# Revit family: Electronics_Desono_Biamp_Full-Range-Surface-Mount-Loudspeaker_KUBO3_KUBO3T
name_source: partatom
category: Communication Devices
units: mm (PartAtom-declared; Revit-internal decimal feet)

## family parameters
Cut with Voids When Loaded = No
Host = Face
Maintain Annotation Orientation = No
OmniClass Number = 23.85.10.11.14.14.14
Part Type = Normal
Room Calculation Point = No
Round Connector Dimension = Use Diameter
Shared = No

## types (4) — shared parameters
Default Elevation = 4' - 0"
Depth = 0' - 4 1/2"
Environmental = IP40 per IEC 60529
Height = 0' - 5"
Input Connection = (2x) 2-way Euroblock connectors for daisy-chaining;connectors accept up to 12 AWG (2.5 mm²)conductors
Manufacturer = Biamp
Mounting Provisions = U-bracket
Nominal Beamwidth  (H x V) = 100° x 100°
Operating Environment = Indoor
Operating Mode = Passive
Operating Range (-10dB) = 115 Hz to 20 kHz
Product Documentation Link = https://downloads.biamp.com
Product Page URL = https://www.biamp.com
Product data url = https://www.bimobject.com
Protection = 3-step self-resetting protection
Transducers = 1 x 3 (76 mm) polypropylene cone
URL = https://www.biamp.com
Width = 0' - 5"

## per-type parameters (varying)
| type | Bracket Material | Connector Description | Continuous Power Handling Nominal Impedance | Controls | Description | Grill Material | Housing Material | Nominal Maximum SPL @ 1m | Nominal Sensitivity @ 1m | Recommended Amplifers | Transformer | Weight |
| KUBO3 B | Biamp - Metal - Black | 2-way Euroblock; 14V 25W 8Ω (100W peak) | 14V; 25W @ 8Ω (100W peak) |  | Desono™ KUBO3 Full Range 3-Inch Surface Mount Loudspeaker | Biamp - Plastic - Black(Grid) | Biamp - Plastic - Black | Peak - 104dB; Continuous - 98dB | 1W - 84dB; 2.83V - 84dB | 25W - 50W @ 8Ω (14V - 20V) |  | 2.20 lb |
| KUBO3 W | Biamp - Metal - White | 2-way Euroblock; 14V 25W 8Ω (100W peak) | 14V; 25W @ 8Ω (100W peak) |  | Desono™ KUBO3 Full Range 3-Inch Surface Mount Loudspeaker | Biamp - Plastic - White(Grid) | Biamp - Plastic - White | Peak - 104dB; Continuous - 98dB | 1W - 84dB; 2.83V - 84dB | 25W - 50W @ 8Ω (14V - 20V) |  | 2.20 lb |
| KUBO3T W | Biamp - Metal - White | 2-way Euroblock; Low impedance 16 ohms, 70V/100V operation | 20V; 25W @ 16Ω (100W peak) | Power tap / low impedance selector switch | Desono™ KUBO3T Full Range 3-Inch Surface Mount Loudspeaker | Biamp - Plastic - White(Grid) | Biamp - Plastic - White | Peak - 106dB; Continuous - 100dB | 1W - 86dB; 2.83V - 83dB | 25W - 50W @ 16Ω (20V - 28V) | 70V: 10W, 5W, 2.5W, 1.25W;100V: 10W, 5W, 2.5W | 2.65 lb |
| KUBO3T B | Biamp - Metal - Black | 2-way Euroblock; Low impedance 16 ohms, 70V/100V operation | 20V; 25W @ 16Ω (100W peak) | Power tap / low impedance selector switch | Desono™ KUBO3T Full Range 3-Inch Surface Mount Loudspeaker | Biamp - Plastic - Black(Grid) | Biamp - Plastic - Black | Peak - 106dB; Continuous - 100dB | 1W - 86dB; 2.83V - 83dB | 25W - 50W @ 16Ω (20V - 28V) | 70V: 10W, 5W, 2.5W, 1.25W;100V: 10W, 5W, 2.5W | 2.65 lb |

note: column(s) folded — value = type name in every type: Model

## geometry (parser evidence)
native form markers: Sweep x4
no freeform markers — native parametric forms only
